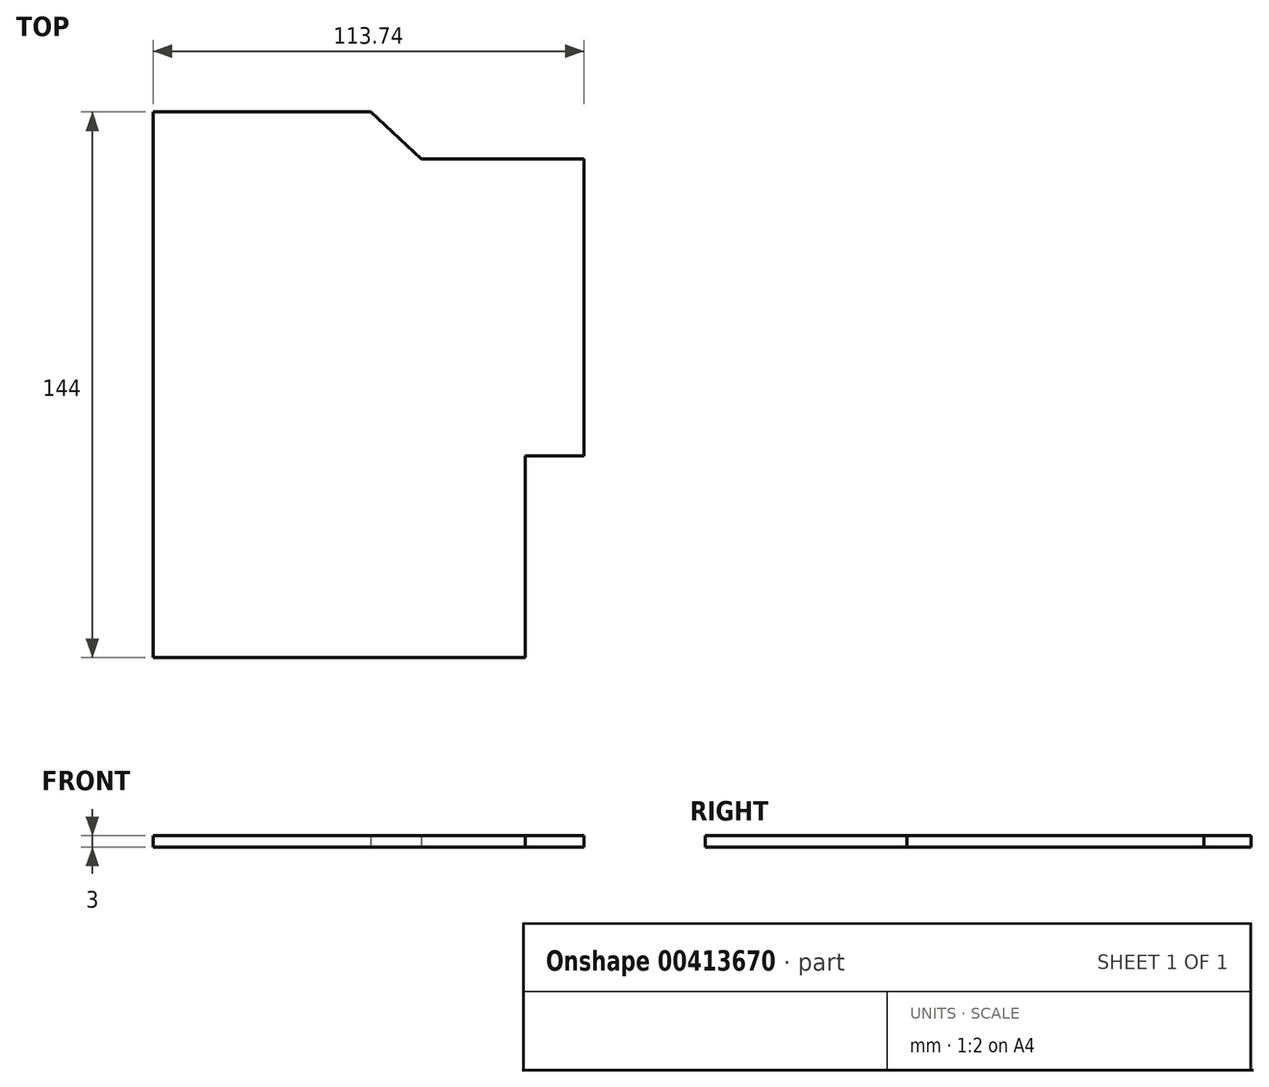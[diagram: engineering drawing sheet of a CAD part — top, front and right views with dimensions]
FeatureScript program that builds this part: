
annotation { "Feature Type Name" : "Feature", "Feature Type Description" : "" }
export const myFeature = defineFeature(function(context is Context, id is Id, definition is map)
    precondition{}
    {
        {
            var Q0;
            Q0=qCreatedBy(makeId("Top.planeOp"),FACE);
            var sketch = newSketch(context, id + "F0", { "sketchPlane" : qUnion([Q0])});
            skLineSegment(sketch, "E0", {"start": v(-70.74, 48.64) * mm, "end": v(-70.74, -95.36) * mm});
            skLineSegment(sketch, "E1", {"start": v(-70.74, -95.36) * mm, "end": v(27.46, -95.36) * mm});
            skLineSegment(sketch, "E2", {"start": v(27.46, -95.36) * mm, "end": v(27.46, -42.2) * mm});
            skLineSegment(sketch, "E3", {"start": v(27.46, -42.2) * mm, "end": v(43, -42.2) * mm});
            skLineSegment(sketch, "E4", {"start": v(43, -42.2) * mm, "end": v(43, 36.2) * mm});
            skLineSegment(sketch, "E5", {"start": v(43, 36.2) * mm, "end": v(0, 36.2) * mm});
            skLineSegment(sketch, "E6", {"start": v(0, 36.2) * mm, "end": v(-13.34, 48.64) * mm});
            skLineSegment(sketch, "E7", {"start": v(-13.34, 48.64) * mm, "end": v(-70.74, 48.64) * mm});
            skSolve(sketch);
        }
        {
            var Q0;
            Q0 = qSketchRegion(id + "F0", true);
            extrude(context, id + "F1", {"entities" : qUnion([Q0]), "depth" : 3 * mm});
        }
    });
